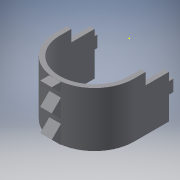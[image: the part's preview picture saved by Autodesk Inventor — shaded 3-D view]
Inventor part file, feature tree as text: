
AUTODESK INVENTOR PART (.ipt)
format: ipt  version: 2016 (Build 200138000, 138)  size: 231,936 bytes
history: native  units: in
note: dims shown in document units (in); Inventor stores cm internally (conversion verified against a paired STEP export)
features: sketch x10, extrude x9, reference x6, projected_geometry x2, plane x1
ambient origin geometry x8: Origin, YZ Plane, XZ Plane, XY Plane, X Axis, Y Axis, Z Axis, Center Point
bodies: Solid1 (feature_tree)
feature tree (28):
  extrude  "Extrusion1"  Depth=1.5in TaperAngle=0.0deg
  extrude  "Extrusion2"  Depth=0.1969in TaperAngle=0.0deg
  extrude  "Extrusion3"  [1 undecoded]
  extrude  "Extrusion4"  Depth=0.3937in
  plane  "Work Plane1"
  sketch  "Sketch5"  dims[d12=1.9685in d14=0.9774in d15=0.3937in d17=1.0in d19=0.5in d20=0.0in]
  extrude  "Extrusion5"  Depth=0.5in TaperAngle=0.0deg
  extrude  "Extrusion6"  Depth=0.197in TaperAngle=0.0deg
  extrude  "Extrusion7"  Depth=0.5in TaperAngle=0.0deg
  extrude  "Extrusion8"  [1 undecoded]
  extrude  "Extrusion9"  [1 undecoded]
  sketch  "Sketch1"  dims[d0=0.1969in d1=1.5in d2=0.0in]
  reference  "Reference1"
  sketch  "Sketch2"  dims[d3=4.6969in d4=0.0in d5=0.1969in d6=0.0in]
  sketch  "Sketch3"  dims[d7=0.1969in d8=0.0in d9=-1.697in]
  sketch  "Sketch4"  dims[d10=0.7874in d11=0.3937in]
  reference  "Reference2"
  sketch  "Sketch6"  dims[d21=0.197in d22=0.0in d23=100.0in d24=0.0in]
  sketch  "Sketch8"  dims[d25=0.5in d26=77.0in d27=0.0in]
  reference  "Reference3"
  reference  "Reference4"
  reference  "Reference5"
  reference  "Reference6"
  sketch  "Sketch9"  dims[d28=0.5in d29=0.0in]
  sketch  "Sketch10"
  sketch  "Sketch11"
  projected_geometry  "Projected Loop1"
  projected_geometry  "Projected Loop2"
note: 3 required parameter values undecoded (feature->parameter linkage not recoverable at this tier; creation-order binding heuristic only, values carry confidence <= 0.55)
